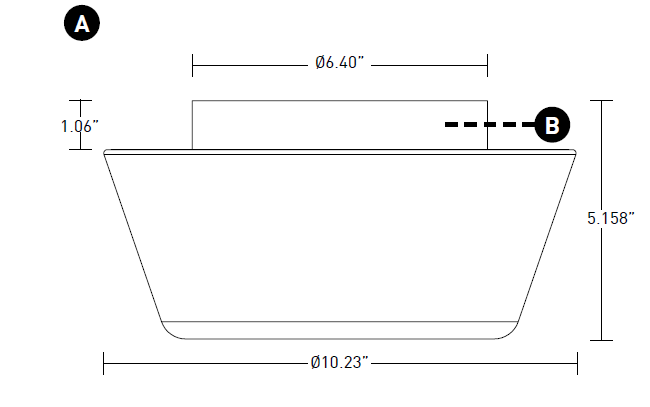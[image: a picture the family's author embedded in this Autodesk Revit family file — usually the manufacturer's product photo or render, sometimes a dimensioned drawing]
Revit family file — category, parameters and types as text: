
# Revit family: Lighting-Accent-Amerlux-2WMACCS
name_source: partatom
category: Lighting Fixtures
revit_build: Autodesk Revit 2017 (Build: 20190508_0315(x64)
units: mm (PartAtom-declared; Revit-internal decimal feet)

## family parameters
Cut with Voids When Loaded = No
Host = Face
Light Source = Yes
Part Type = Normal
Room Calculation Point = No
Round Connector Dimension = Use Diameter
Shared = No

## types (1)
- Lighting-Accent-Amerlux-2WMACCS
    Apparent Load = 0 VA
    Color Filter = 16777215
    Cross Bar Length = 24"
    Default Elevation = 48"
    Description = Small Wall Mount Accent
    Dimming Lamp Color Temperature Shift = <None>
    Emit Shape Visible in Rendering = Yes
    Emit from Circle Diameter = 2"
    Lamp = LED
    Manufacturer = Amerlux
    Material = Black Finish
    Model = 2WMACCS
    Number of Poles = 1
    Photometric Web File = generic
    Power Factor = 1
    Tilt Angle = 45.00°
    URL = http://www.amerlux.com
    Voltage = 0 V

## geometry (parser evidence)
native form markers: Blend x18, Sweep x5
no freeform markers — native parametric forms only
